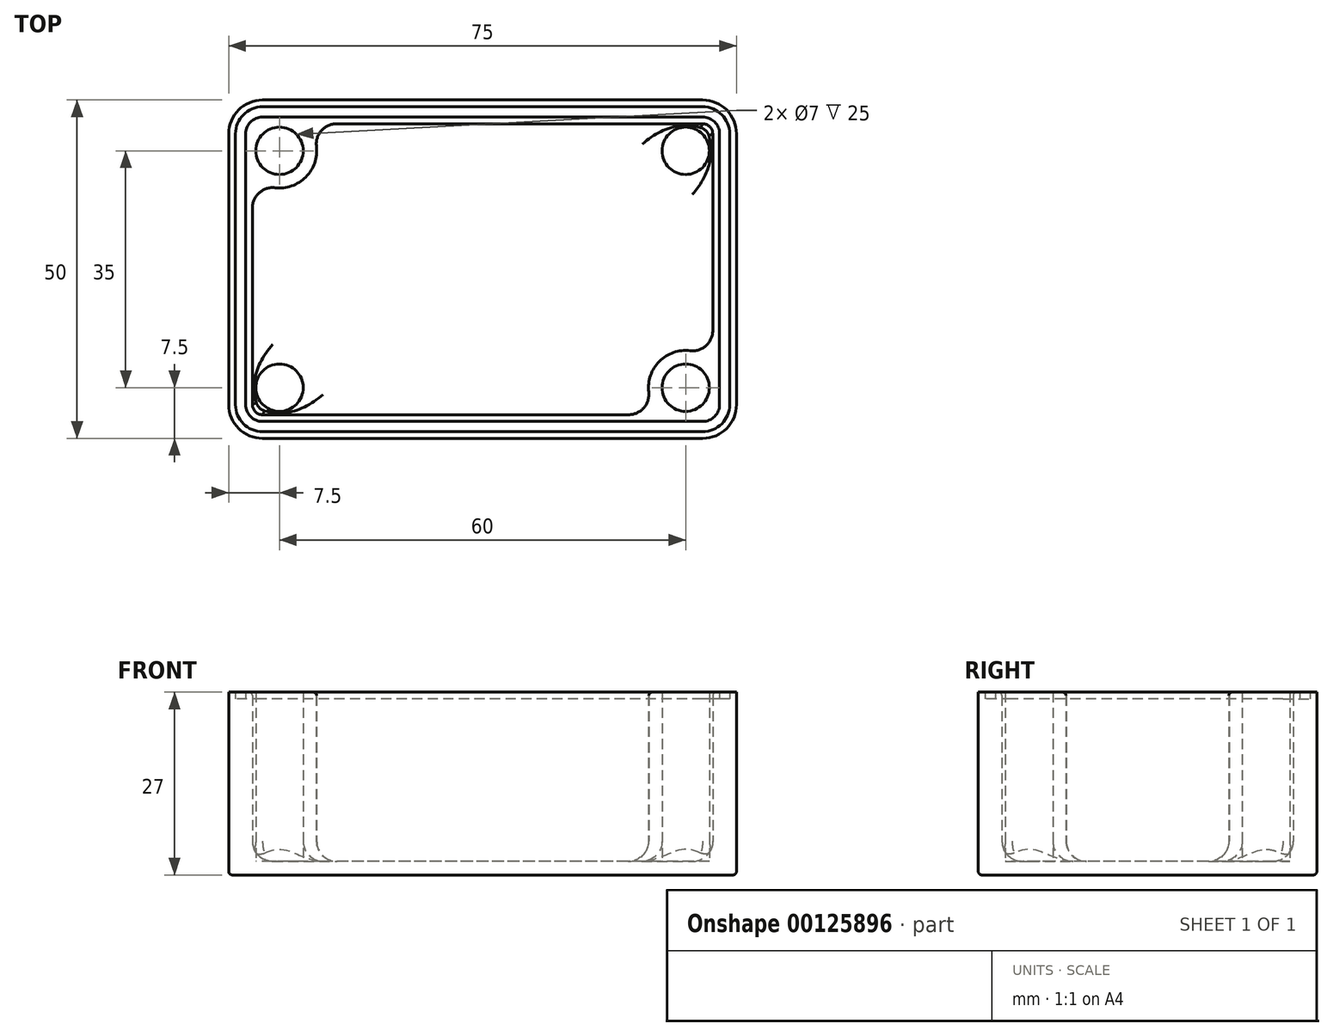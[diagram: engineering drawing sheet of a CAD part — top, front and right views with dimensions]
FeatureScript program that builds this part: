
annotation { "Feature Type Name" : "Feature", "Feature Type Description" : "" }
export const myFeature = defineFeature(function(context is Context, id is Id, definition is map)
    precondition{}
    {
        {
            var Q0;
            Q0=qCreatedBy(makeId("Top.planeOp"),FACE);
            var sketch = newSketch(context, id + "F0", { "sketchPlane" : qUnion([Q0])});
            skLineSegment(sketch, "E0.bottom", {"start": v(32.5, 25) * mm, "end": v(-32.5, 25) * mm});
            skLineSegment(sketch, "E0.top", {"start": v(32.5, -25) * mm, "end": v(-32.5, -25) * mm});
            skLineSegment(sketch, "E0.left", {"start": v(37.5, 20) * mm, "end": v(37.5, -20) * mm});
            skLineSegment(sketch, "E0.right", {"start": v(-37.5, 20) * mm, "end": v(-37.5, -20) * mm});
            skPoint(sketch, "E0.middle", {"position": v(0, 0) * mm});
            skCircle(sketch, "E1", {"center": v(-30, 17.5) * mm, "radius": 3.5 * mm});
            skLineSegment(sketch, "E2", {"start": v(0, 0) * mm, "end": v(0, 25) * mm, "construction": true});
            skLineSegment(sketch, "E3", {"start": v(0, 0) * mm, "end": v(0, -25) * mm, "construction": true});
            skLineSegment(sketch, "E4", {"start": v(0, 0) * mm, "end": v(37.5, 0) * mm, "construction": true});
            skLineSegment(sketch, "E5", {"start": v(0, 0) * mm, "end": v(-37.5, 0) * mm, "construction": true});
            skCircle(sketch, "E6.MirrorC", {"center": v(-30, -17.5) * mm, "radius": 3.5 * mm});
            skCircle(sketch, "E7.MirrorC", {"center": v(30, 17.5) * mm, "radius": 3.5 * mm});
            skCircle(sketch, "E8.MirrorC", {"center": v(30, -17.5) * mm, "radius": 3.5 * mm});
            skPoint(sketch, "E9.visualSharp", {"position": v(-37.5, 25) * mm});
            skArc(sketch, "E9.filletArc", {"start": v(-32.5, 25) * mm, "mid": v(-36.04, 23.54) * mm, "end": v(-37.5, 20) * mm});
            skPoint(sketch, "E10.visualSharp", {"position": v(37.5, 25) * mm});
            skArc(sketch, "E10.filletArc", {"start": v(37.5, 20) * mm, "mid": v(36.04, 23.54) * mm, "end": v(32.5, 25) * mm});
            skPoint(sketch, "E11.visualSharp", {"position": v(37.5, -25) * mm});
            skArc(sketch, "E11.filletArc", {"start": v(32.5, -25) * mm, "mid": v(36.04, -23.54) * mm, "end": v(37.5, -20) * mm});
            skPoint(sketch, "E12.visualSharp", {"position": v(-37.5, -25) * mm});
            skArc(sketch, "E12.filletArc", {"start": v(-37.5, -20) * mm, "mid": v(-36.04, -23.54) * mm, "end": v(-32.5, -25) * mm});
            skArc(sketch, "E13.0", {"start": v(36.5, 20) * mm, "mid": v(35.33, 22.83) * mm, "end": v(32.5, 24) * mm});
            skLineSegment(sketch, "E13.1", {"start": v(36.5, 20) * mm, "end": v(36.5, -20) * mm});
            skLineSegment(sketch, "E13.2", {"start": v(32.5, 24) * mm, "end": v(-32.5, 24) * mm});
            skArc(sketch, "E13.3", {"start": v(32.5, -24) * mm, "mid": v(35.33, -22.83) * mm, "end": v(36.5, -20) * mm});
            skArc(sketch, "E13.4", {"start": v(-32.5, 24) * mm, "mid": v(-35.33, 22.83) * mm, "end": v(-36.5, 20) * mm});
            skLineSegment(sketch, "E13.5", {"start": v(-36.5, 20) * mm, "end": v(-36.5, -20) * mm});
            skArc(sketch, "E13.6", {"start": v(-36.5, -20) * mm, "mid": v(-35.33, -22.83) * mm, "end": v(-32.5, -24) * mm});
            skLineSegment(sketch, "E13.7", {"start": v(32.5, -24) * mm, "end": v(-32.5, -24) * mm});
            skArc(sketch, "E14.0", {"start": v(35, 20) * mm, "mid": v(34.27, 21.77) * mm, "end": v(32.5, 22.5) * mm});
            skLineSegment(sketch, "E14.1", {"start": v(35, 20) * mm, "end": v(35, -20) * mm});
            skLineSegment(sketch, "E14.2", {"start": v(32.5, 22.5) * mm, "end": v(-32.5, 22.5) * mm});
            skArc(sketch, "E14.3", {"start": v(32.5, -22.5) * mm, "mid": v(34.27, -21.77) * mm, "end": v(35, -20) * mm});
            skArc(sketch, "E14.4", {"start": v(-32.5, 22.5) * mm, "mid": v(-34.27, 21.77) * mm, "end": v(-35, 20) * mm});
            skLineSegment(sketch, "E14.5", {"start": v(-35, 20) * mm, "end": v(-35, -20) * mm});
            skArc(sketch, "E14.6", {"start": v(-35, -20) * mm, "mid": v(-34.27, -21.77) * mm, "end": v(-32.5, -22.5) * mm});
            skLineSegment(sketch, "E14.7", {"start": v(32.5, -22.5) * mm, "end": v(-32.5, -22.5) * mm});
            skArc(sketch, "E15.0", {"start": v(34, 20) * mm, "mid": v(33.56, 21.06) * mm, "end": v(32.5, 21.5) * mm});
            skLineSegment(sketch, "E15.1", {"start": v(34, 20) * mm, "end": v(34, -20) * mm});
            skLineSegment(sketch, "E15.2", {"start": v(32.5, 21.5) * mm, "end": v(-32.5, 21.5) * mm});
            skArc(sketch, "E15.3", {"start": v(32.5, -21.5) * mm, "mid": v(33.56, -21.06) * mm, "end": v(34, -20) * mm});
            skArc(sketch, "E15.4", {"start": v(-32.5, 21.5) * mm, "mid": v(-33.56, 21.06) * mm, "end": v(-34, 20) * mm});
            skLineSegment(sketch, "E15.5", {"start": v(-34, 20) * mm, "end": v(-34, -20) * mm});
            skArc(sketch, "E15.6", {"start": v(-34, -20) * mm, "mid": v(-33.56, -21.06) * mm, "end": v(-32.5, -21.5) * mm});
            skLineSegment(sketch, "E15.7", {"start": v(32.5, -21.5) * mm, "end": v(-32.5, -21.5) * mm});
            skArc(sketch, "E16.0", {"start": v(-34, 13.73) * mm, "mid": v(-26.11, 13.61) * mm, "end": v(-26.23, 21.5) * mm});
            skArc(sketch, "E17.MirrorCS", {"start": v(34, 13.73) * mm, "mid": v(26.11, 13.61) * mm, "end": v(26.23, 21.5) * mm});
            skArc(sketch, "E18.MirrorCS", {"start": v(-34, -13.73) * mm, "mid": v(-26.11, -13.61) * mm, "end": v(-26.23, -21.5) * mm});
            skArc(sketch, "E19.MirrorCS", {"start": v(34, -13.73) * mm, "mid": v(26.11, -13.61) * mm, "end": v(26.23, -21.5) * mm});
            skSolve(sketch);
        }
        {
            var Q0;
            Q0=makeQuery(id+"F0.imprint","IMPRINT",FACE,{"disambiguationData":[TD([[makeQuery(id+"F0.imprint","IMPRINT",EDGE,{"derivedFrom":sQuery(id+"F0.wireOp",EDGE,"E0.bottom")}),1.0]])]});
            var Q1;
            Q1=makeQuery(id+"F0.imprint","IMPRINT",FACE,{"disambiguationData":[TD([[makeQuery(id+"F0.imprint","IMPRINT",EDGE,{"derivedFrom":sQuery(id+"F0.wireOp",EDGE,"E6.MirrorC")}),-1.0]])]});
            var Q2;
            {var subQ0=sQuery(id+"F0.wireOp",EDGE,"E16.0");Q2=makeQuery(id+"F0.imprint","IMPRINT",FACE,{"disambiguationData":[TD([[makeQuery(id+"F0.imprint","IMPRINT",EDGE,{"derivedFrom":subQ0}),-1.0]])]});}
            var Q3;
            Q3=makeQuery(id+"F0.imprint","IMPRINT",FACE,{"disambiguationData":[TD([[makeQuery(id+"F0.imprint","IMPRINT",EDGE,{"derivedFrom":sQuery(id+"F0.wireOp",EDGE,"E7.MirrorC")}),-1.0]])]});
            var Q4;
            Q4=makeQuery(id+"F0.imprint","IMPRINT",FACE,{"disambiguationData":[TD([[makeQuery(id+"F0.imprint","IMPRINT",EDGE,{"derivedFrom":sQuery(id+"F0.wireOp",EDGE,"E14.0")}),1.0]])]});
            var Q5;
            Q5=makeQuery(id+"F0.imprint","IMPRINT",FACE,{"disambiguationData":[TD([[makeQuery(id+"F0.imprint","IMPRINT",EDGE,{"derivedFrom":sQuery(id+"F0.wireOp",EDGE,"E7.MirrorC")}),1.0]])]});
            var Q6;
            Q6=makeQuery(id+"F0.imprint","IMPRINT",FACE,{"disambiguationData":[TD([[makeQuery(id+"F0.imprint","IMPRINT",EDGE,{"derivedFrom":sQuery(id+"F0.wireOp",EDGE,"E8.MirrorC")}),1.0]])]});
            var Q7;
            Q7=makeQuery(id+"F0.imprint","IMPRINT",FACE,{"disambiguationData":[TD([[makeQuery(id+"F0.imprint","IMPRINT",EDGE,{"derivedFrom":sQuery(id+"F0.wireOp",EDGE,"E13.0")}),1.0]])]});
            var Q8;
            Q8=makeQuery(id+"F0.imprint","IMPRINT",FACE,{"disambiguationData":[TD([[makeQuery(id+"F0.imprint","IMPRINT",EDGE,{"derivedFrom":sQuery(id+"F0.wireOp",EDGE,"E8.MirrorC")}),-1.0]])]});
            var Q9;
            Q9=makeQuery(id+"F0.imprint","IMPRINT",FACE,{"disambiguationData":[TD([[makeQuery(id+"F0.imprint","IMPRINT",EDGE,{"derivedFrom":sQuery(id+"F0.wireOp",EDGE,"E6.MirrorC")}),1.0]])]});
            var Q10;
            Q10=makeQuery(id+"F0.imprint","IMPRINT",FACE,{"disambiguationData":[TD([[makeQuery(id+"F0.imprint","IMPRINT",EDGE,{"derivedFrom":sQuery(id+"F0.wireOp",EDGE,"E1")}),1.0]])]});
            var Q11;
            Q11=makeQuery(id+"F0.imprint","IMPRINT",FACE,{"disambiguationData":[TD([[makeQuery(id+"F0.imprint","IMPRINT",EDGE,{"derivedFrom":sQuery(id+"F0.wireOp",EDGE,"E1")}),-1.0]])]});
            extrude(context, id + "F1", {"entities" : qUnion([Q0, Q1, Q2, Q3, Q4, Q5, Q6, Q7, Q8, Q9, Q10, Q11]), "oppositeDirection" : true, "depth" : 2 * mm});
        }
        {
            var Q0;
            Q0 = qSketchRegion(id + "F0", true);
            var Q1;
            Q1=makeQuery(id+"F0.imprint","IMPRINT",FACE,{"disambiguationData":[TD([[makeQuery(id+"F0.imprint","IMPRINT",EDGE,{"derivedFrom":sQuery(id+"F0.wireOp",EDGE,"E6.MirrorC")}),1.0]])]});
            var Q2;
            Q2=makeQuery(id+"F0.imprint","IMPRINT",FACE,{"disambiguationData":[TD([[makeQuery(id+"F0.imprint","IMPRINT",EDGE,{"derivedFrom":sQuery(id+"F0.wireOp",EDGE,"E14.0")}),1.0]])]});
            var Q3;
            Q3=makeQuery(id+"F0.imprint","IMPRINT",FACE,{"disambiguationData":[TD([[makeQuery(id+"F0.imprint","IMPRINT",EDGE,{"derivedFrom":sQuery(id+"F0.wireOp",EDGE,"E7.MirrorC")}),1.0]])]});
            var Q4;
            Q4=makeQuery(id+"F0.imprint","IMPRINT",FACE,{"disambiguationData":[TD([[makeQuery(id+"F0.imprint","IMPRINT",EDGE,{"derivedFrom":sQuery(id+"F0.wireOp",EDGE,"E8.MirrorC")}),-1.0]])]});
            var Q5;
            Q5=makeQuery(id+"F0.imprint","IMPRINT",FACE,{"disambiguationData":[TD([[makeQuery(id+"F0.imprint","IMPRINT",EDGE,{"derivedFrom":sQuery(id+"F0.wireOp",EDGE,"E1")}),-1.0]])]});
            extrude(context, id + "F2", {"entities" : qUnion([Q0, Q1, Q2, Q3, Q4, Q5]), "operationType" : NewBodyOperationType.ADD, "depth" : 25 * mm});
        }
        {
            var Q0;
            Q0=makeQuery(id+"F0.imprint","IMPRINT",FACE,{"disambiguationData":[TD([[makeQuery(id+"F0.imprint","IMPRINT",EDGE,{"derivedFrom":sQuery(id+"F0.wireOp",EDGE,"E13.0")}),1.0]])]});
            extrude(context, id + "F3", {"entities" : qUnion([Q0]), "operationType" : NewBodyOperationType.ADD, "depth" : 24 * mm});
        }
        {
            var Q0;
            Q0=makeQuery(id+"F2.boolean.opBoolean","SPLIT",FACE,{"disambiguationData":[TD([makeQuery(id+"F2.opExtrude","SWEPT_FACE",FACE,{"disambiguationData":[OSD([sQuery(id+"F0.wireOp",EDGE,"E15.1")])]})])],"derivedFrom":makeQuery(id+"F1.opExtrude","CAP_FACE",FACE,{"disambiguationData":[OSD([sQuery(id+"F0.wireOp",EDGE,"E0.bottom"),sQuery(id+"F0.wireOp",EDGE,"E0.top"),sQuery(id+"F0.wireOp",EDGE,"E0.left"),sQuery(id+"F0.wireOp",EDGE,"E0.right"),sQuery(id+"F0.wireOp",EDGE,"E9.filletArc"),sQuery(id+"F0.wireOp",EDGE,"E10.filletArc"),sQuery(id+"F0.wireOp",EDGE,"E11.filletArc"),sQuery(id+"F0.wireOp",EDGE,"E12.filletArc")])],"isStart":true})});
            var Q1;
            Q1=makeQuery(id+"F2.opExtrude","SWEPT_EDGE",EDGE,{"disambiguationData":[OSD([sQuery(id+"F0.wireOp",EDGE,"E15.2"),sQuery(id+"F0.wireOp",EDGE,"E16.0")])]});
            var Q2;
            Q2=makeQuery(id+"F2.opExtrude","SWEPT_EDGE",EDGE,{"disambiguationData":[OSD([sQuery(id+"F0.wireOp",EDGE,"E15.5"),sQuery(id+"F0.wireOp",EDGE,"E16.0")])]});
            var Q3;
            Q3=makeQuery(id+"F2.opExtrude","SWEPT_EDGE",EDGE,{"disambiguationData":[OSD([sQuery(id+"F0.wireOp",EDGE,"E15.2"),sQuery(id+"F0.wireOp",EDGE,"E17.MirrorCS")])]});
            var Q4;
            Q4=makeQuery(id+"F2.opExtrude","SWEPT_EDGE",EDGE,{"disambiguationData":[OSD([sQuery(id+"F0.wireOp",EDGE,"E15.1"),sQuery(id+"F0.wireOp",EDGE,"E17.MirrorCS")])]});
            var Q5;
            Q5=makeQuery(id+"F2.opExtrude","SWEPT_EDGE",EDGE,{"disambiguationData":[OSD([sQuery(id+"F0.wireOp",EDGE,"E15.7"),sQuery(id+"F0.wireOp",EDGE,"E19.MirrorCS")])]});
            var Q6;
            Q6=makeQuery(id+"F2.opExtrude","SWEPT_EDGE",EDGE,{"disambiguationData":[OSD([sQuery(id+"F0.wireOp",EDGE,"E15.1"),sQuery(id+"F0.wireOp",EDGE,"E19.MirrorCS")])]});
            var Q7;
            Q7=makeQuery(id+"F2.opExtrude","SWEPT_EDGE",EDGE,{"disambiguationData":[OSD([sQuery(id+"F0.wireOp",EDGE,"E15.7"),sQuery(id+"F0.wireOp",EDGE,"E18.MirrorCS")])]});
            var Q8;
            Q8=makeQuery(id+"F2.opExtrude","SWEPT_EDGE",EDGE,{"disambiguationData":[OSD([sQuery(id+"F0.wireOp",EDGE,"E15.5"),sQuery(id+"F0.wireOp",EDGE,"E18.MirrorCS")])]});
            fillet(context, id + "F4", {"entities" : qUnion([Q0, Q1, Q2, Q3, Q4, Q5, Q6, Q7, Q8]), "radius" : 3 * mm, "tangentPropagation" : true, "allowEdgeOverflow" : false});
        }
        {
            var Q0;
            Q0=makeQuery(id+"F2.opExtrude","CAP_EDGE",EDGE,{"disambiguationData":[OSD([sQuery(id+"F0.wireOp",EDGE,"E16.0")])],"isStart":false});
            fillet(context, id + "F5", {"entities" : qUnion([Q0]), "radius" : .5 * mm, "tangentPropagation" : true, "allowEdgeOverflow" : false});
        }
        {
            var Q0;
            Q0=makeQuery(id+"F1.opExtrude","CAP_FACE",FACE,{"disambiguationData":[OSD([sQuery(id+"F0.wireOp",EDGE,"E0.bottom"),sQuery(id+"F0.wireOp",EDGE,"E0.top"),sQuery(id+"F0.wireOp",EDGE,"E0.left"),sQuery(id+"F0.wireOp",EDGE,"E0.right"),sQuery(id+"F0.wireOp",EDGE,"E9.filletArc"),sQuery(id+"F0.wireOp",EDGE,"E10.filletArc"),sQuery(id+"F0.wireOp",EDGE,"E11.filletArc"),sQuery(id+"F0.wireOp",EDGE,"E12.filletArc")])],"isStart":false});
            fillet(context, id + "F6", {"entities" : qUnion([Q0]), "radius" : .5 * mm, "tangentPropagation" : true, "allowEdgeOverflow" : false});
        }
    });
